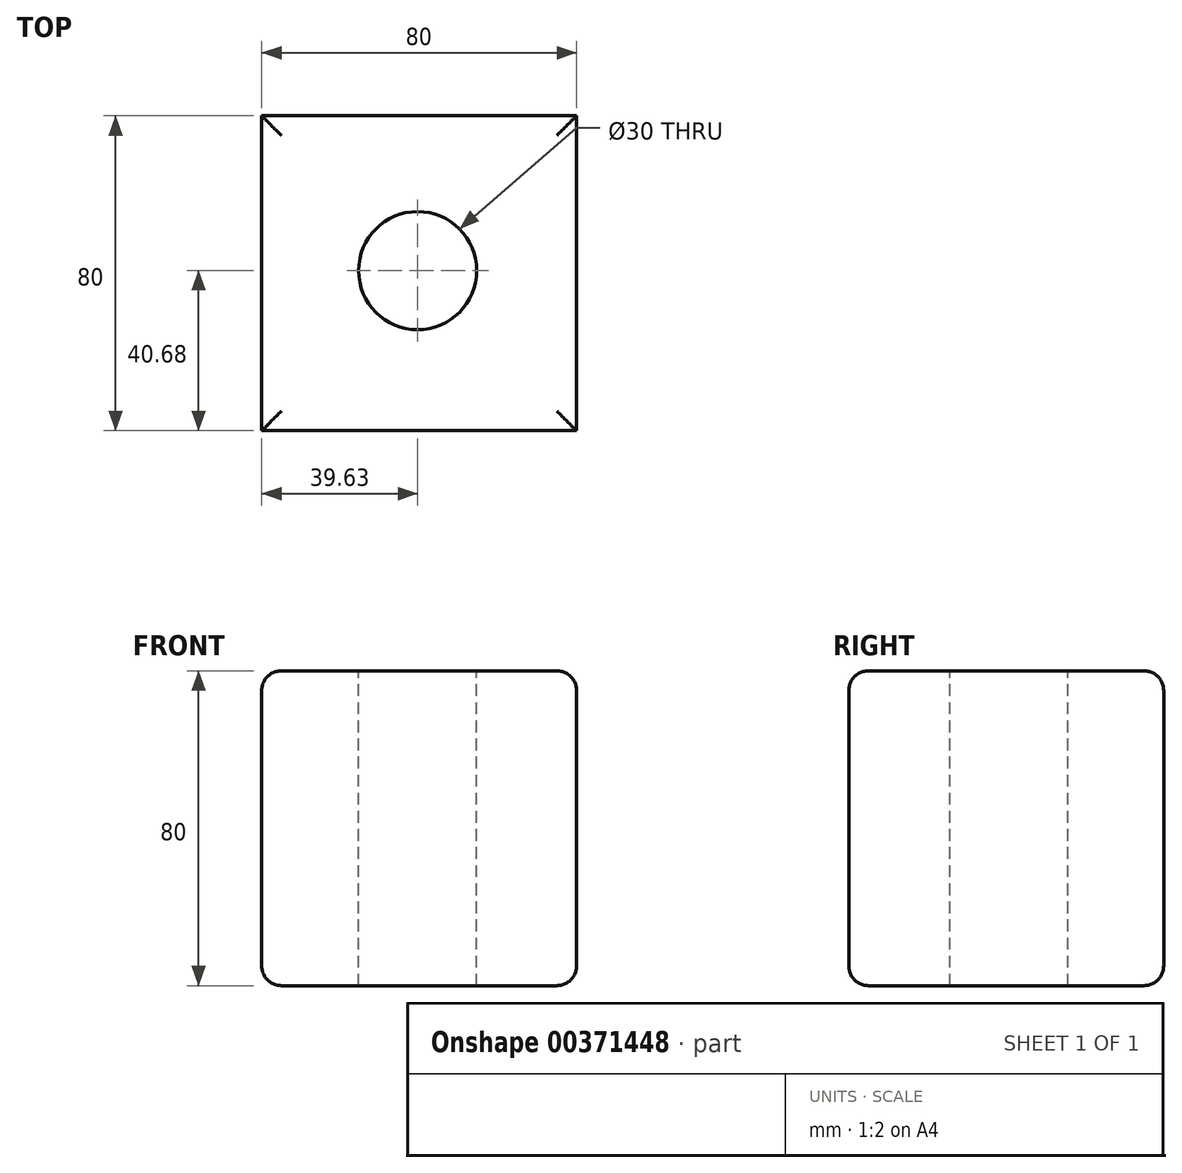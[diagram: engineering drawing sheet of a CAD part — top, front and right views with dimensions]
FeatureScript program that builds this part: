
annotation { "Feature Type Name" : "Feature", "Feature Type Description" : "" }
export const myFeature = defineFeature(function(context is Context, id is Id, definition is map)
    precondition{}
    {
        {
            var Q0;
            Q0=qCreatedBy(makeId("Top.planeOp"),FACE);
            var sketch = newSketch(context, id + "F0", { "sketchPlane" : qUnion([Q0])});
            skLineSegment(sketch, "E0.bottom", {"start": v(-54.93, 54.17) * mm, "end": v(25.07, 54.17) * mm});
            skLineSegment(sketch, "E0.top", {"start": v(-54.93, -25.83) * mm, "end": v(25.07, -25.83) * mm});
            skLineSegment(sketch, "E0.left", {"start": v(-54.93, 54.17) * mm, "end": v(-54.93, -25.83) * mm});
            skLineSegment(sketch, "E0.right", {"start": v(25.07, 54.17) * mm, "end": v(25.07, -25.83) * mm});
            skSolve(sketch);
        }
        {
            var Q0;
            Q0 = qSketchRegion(id + "F0", true);
            extrude(context, id + "F1", {"entities" : qUnion([Q0]), "depth" : 80 * mm});
        }
        {
            var Q0;
            Q0=makeQuery(id+"F1.opExtrude","CAP_FACE",FACE,{"disambiguationData":[OSD([sQuery(id+"F0.wireOp",EDGE,"E0.bottom"),sQuery(id+"F0.wireOp",EDGE,"E0.top"),sQuery(id+"F0.wireOp",EDGE,"E0.left"),sQuery(id+"F0.wireOp",EDGE,"E0.right")])],"isStart":false});
            var sketch = newSketch(context, id + "F2", { "sketchPlane" : qUnion([Q0])});
            skCircle(sketch, "E1", {"center": v(-15.3, 14.85) * mm, "radius": 15 * mm});
            skSolve(sketch);
        }
        {
            var Q0;
            Q0=makeQuery(id+"F2.imprint","IMPRINT",FACE,{"disambiguationData":[TD([[makeQuery(id+"F2.imprint","IMPRINT",EDGE,{"derivedFrom":sQuery(id+"F2.wireOp",EDGE,"E1")}),1.0]])]});
            extrude(context, id + "F3", {"entities" : qUnion([Q0]), "operationType" : NewBodyOperationType.REMOVE, "endBound" : BoundingType.THROUGH_ALL, "oppositeDirection" : true, "depth" : 25 * mm});
        }
        {
            var Q0;
            Q0=makeQuery(id+"F1.opExtrude","CAP_EDGE",EDGE,{"disambiguationData":[OSD([sQuery(id+"F0.wireOp",EDGE,"E0.top")])],"isStart":true});
            var Q1;
            Q1=makeQuery(id+"F1.opExtrude","CAP_EDGE",EDGE,{"disambiguationData":[OSD([sQuery(id+"F0.wireOp",EDGE,"E0.left")])],"isStart":true});
            var Q2;
            Q2=makeQuery(id+"F1.opExtrude","CAP_EDGE",EDGE,{"disambiguationData":[OSD([sQuery(id+"F0.wireOp",EDGE,"E0.right")])],"isStart":true});
            var Q3;
            Q3=makeQuery(id+"F1.opExtrude","CAP_EDGE",EDGE,{"disambiguationData":[OSD([sQuery(id+"F0.wireOp",EDGE,"E0.bottom")])],"isStart":true});
            fillet(context, id + "F4", {"entities" : qUnion([Q0, Q1, Q2, Q3]), "radius" : 5 * mm, "tangentPropagation" : true, "allowEdgeOverflow" : false});
        }
        {
            var Q0;
            Q0=makeQuery(id+"F1.opExtrude","CAP_EDGE",EDGE,{"disambiguationData":[OSD([sQuery(id+"F0.wireOp",EDGE,"E0.bottom")])],"isStart":false});
            var Q1;
            Q1=makeQuery(id+"F1.opExtrude","CAP_EDGE",EDGE,{"disambiguationData":[OSD([sQuery(id+"F0.wireOp",EDGE,"E0.left")])],"isStart":false});
            var Q2;
            Q2=makeQuery(id+"F1.opExtrude","CAP_EDGE",EDGE,{"disambiguationData":[OSD([sQuery(id+"F0.wireOp",EDGE,"E0.top")])],"isStart":false});
            var Q3;
            Q3=makeQuery(id+"F1.opExtrude","CAP_EDGE",EDGE,{"disambiguationData":[OSD([sQuery(id+"F0.wireOp",EDGE,"E0.right")])],"isStart":false});
            fillet(context, id + "F5", {"entities" : qUnion([Q0, Q1, Q2, Q3]), "radius" : 5 * mm, "tangentPropagation" : true, "allowEdgeOverflow" : false});
        }
    });
